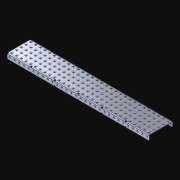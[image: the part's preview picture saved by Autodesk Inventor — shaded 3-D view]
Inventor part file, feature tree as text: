
AUTODESK INVENTOR PART (.ipt)
format: ipt  version: 2021 (Build 250183000, 183)  size: 2,331,648 bytes
history: native  units: in
note: dims shown in document units (in); Inventor stores cm internally (conversion verified against a paired STEP export)
features: extrude x211, other x211, sketch x4, pattern_linear x3
ambient origin geometry x8: Origin, YZ Plane, XZ Plane, XY Plane, X Axis, Y Axis, Z Axis, Center Point
bodies: Solid1 (feature_tree)
feature tree (429):
  pattern_linear  "Rectangular Pattern1"  Spacing1=0.182in  [1 undecoded]
  pattern_linear  "Rectangular Pattern2"  Spacing1=0.046in  [1 undecoded]
  pattern_linear  "Rectangular Pattern3"  Spacing1=0.5in  [1 undecoded]
  extrude  "Extrusion1"  Depth=0.046in
  sketch  "Sketch1"  dims[d0=0.182in]
  other  "Srf1"
  sketch  "Sketch2"  dims[d1=0.046in d2=0.0in]
  other  "Srf2"
  sketch  "Sketch3"  dims[d3=0.182in]
  other  "Srf3"
  other  "Srf4"
  other  "Srf5"
  other  "Srf6"
  other  "Srf7"
  other  "Srf8"
  other  "Srf9"
  other  "Srf10"
  other  "Srf11"
  other  "Srf12"
  other  "Srf13"
  other  "Srf14"
  other  "Srf15"
  other  "Srf16"
  other  "Srf17"
  other  "Srf18"
  other  "Srf19"
  other  "Srf20"
  other  "Srf21"
  other  "Srf22"
  other  "Srf23"
  other  "Srf24"
  other  "Srf25"
  other  "Srf26"
  other  "Srf27"
  other  "Srf28"
  other  "Srf29"
  other  "Srf30"
  other  "Srf31"
  other  "Srf32"
  other  "Srf38"
  other  "Srf39"
  other  "Srf40"
  other  "Srf41"
  other  "Srf42"
  other  "Srf43"
  other  "Srf44"
  other  "Srf45"
  other  "Srf46"
  other  "Srf47"
  other  "Srf48"
  other  "Srf49"
  other  "Srf50"
  other  "Srf51"
  other  "Srf52"
  other  "Srf53"
  other  "Srf54"
  other  "Srf55"
  other  "Srf56"
  other  "Srf57"
  other  "Srf58"
  other  "Srf59"
  other  "Srf60"
  other  "Srf61"
  other  "Srf62"
  other  "Srf63"
  other  "Srf64"
  other  "Srf65"
  other  "Srf66"
  other  "Srf72"
  other  "Srf73"
  other  "Srf74"
  other  "Srf75"
  other  "Srf76"
  other  "Srf77"
  other  "Srf78"
  other  "Srf79"
  other  "Srf80"
  other  "Srf81"
  other  "Srf82"
  other  "Srf83"
  other  "Srf84"
  other  "Srf85"
  other  "Srf86"
  other  "Srf87"
  other  "Srf88"
  other  "Srf89"
  other  "Srf90"
  other  "Srf91"
  other  "Srf92"
  other  "Srf93"
  other  "Srf94"
  other  "Srf95"
  other  "Srf96"
  other  "Srf97"
  other  "Srf98"
  other  "Srf99"
  other  "Srf100"
  other  "Srf101"
  other  "Srf107"
  other  "Srf108"
  other  "Srf109"
  other  "Srf110"
  other  "Srf111"
  other  "Srf112"
  other  "Srf113"
  other  "Srf114"
  other  "Srf115"
  other  "Srf116"
  other  "Srf117"
  other  "Srf118"
  other  "Srf119"
  other  "Srf120"
  other  "Srf121"
  other  "Srf122"
  other  "Srf123"
  other  "Srf124"
  other  "Srf125"
  other  "Srf126"
  other  "Srf127"
  other  "Srf128"
  other  "Srf129"
  other  "Srf130"
  other  "Srf131"
  other  "Srf132"
  other  "Srf133"
  other  "Srf134"
  other  "Srf135"
  other  "Srf136"
  other  "Srf142"
  other  "Srf143"
  other  "Srf144"
  other  "Srf145"
  other  "Srf146"
  other  "Srf147"
  other  "Srf148"
  other  "Srf149"
  other  "Srf150"
  other  "Srf151"
  other  "Srf152"
  other  "Srf153"
  other  "Srf154"
  other  "Srf155"
  other  "Srf156"
  other  "Srf157"
  other  "Srf158"
  other  "Srf159"
  other  "Srf160"
  other  "Srf161"
  other  "Srf162"
  other  "Srf163"
  other  "Srf164"
  other  "Srf165"
  other  "Srf166"
  other  "Srf167"
  other  "Srf168"
  other  "Srf169"
  other  "Srf170"
  other  "Srf171"
  other  "Srf177"
  other  "Srf178"
  other  "Srf179"
  other  "Srf180"
  other  "Srf181"
  other  "Srf182"
  other  "Srf183"
  other  "Srf184"
  other  "Srf185"
  other  "Srf186"
  other  "Srf187"
  other  "Srf188"
  other  "Srf189"
  other  "Srf190"
  other  "Srf191"
  other  "Srf192"
  other  "Srf193"
  other  "Srf194"
  other  "Srf195"
  other  "Srf196"
  other  "Srf197"
  other  "Srf198"
  other  "Srf199"
  other  "Srf200"
  other  "Srf201"
  other  "Srf202"
  other  "Srf203"
  other  "Srf204"
  other  "Srf205"
  other  "Srf206"
  other  "Srf212"
  other  "Srf213"
  other  "Srf214"
  other  "Srf215"
  other  "Srf216"
  other  "Srf217"
  other  "Srf218"
  other  "Srf219"
  other  "Srf220"
  other  "Srf221"
  other  "Srf222"
  other  "Srf223"
  other  "Srf224"
  other  "Srf225"
  other  "Srf226"
  other  "Srf227"
  other  "Srf228"
  other  "Srf229"
  other  "Srf230"
  other  "Srf231"
  other  "Srf232"
  other  "Srf233"
  other  "Srf234"
  other  "Srf235"
  other  "Srf236"
  other  "Srf237"
  other  "Srf238"
  other  "Srf239"
  other  "Srf240"
  sketch  "Sketch4"  dims[d4=0.046in d5=0.0in d6=0.182in d7=0.046in d8=0.0in d11=0.5in d12=11.811in d14=0.5in d15=1.9685in d17=0.5in d18=11.811in d20=0.5in d21=2.5in d22=0.0in]
  parser-record x1  (decoder bookkeeping rows leaked as tree rows — omitted from the tree; the rows remain in map.json)
  extrude  "ExtrusionSrf1"  Depth=0.046in
  extrude  "ExtrusionSrf2"  Depth=0.046in
  extrude  "ExtrusionSrf3"  Depth=0.046in
  extrude  "ExtrusionSrf4"  Depth=0.046in
  extrude  "ExtrusionSrf5"  Depth=0.046in
  extrude  "ExtrusionSrf6"  TaperAngle=0.0deg  [1 undecoded]
  extrude  "ExtrusionSrf7"  [1 undecoded]
  extrude  "ExtrusionSrf8"  [1 undecoded]
  extrude  "ExtrusionSrf9"  [1 undecoded]
  extrude  "ExtrusionSrf10"  [1 undecoded]
  extrude  "ExtrusionSrf11"  [1 undecoded]
  extrude  "ExtrusionSrf12"  [1 undecoded]
  extrude  "ExtrusionSrf13"  [1 undecoded]
  extrude  "ExtrusionSrf14"  [1 undecoded]
  extrude  "ExtrusionSrf15"  [1 undecoded]
  extrude  "ExtrusionSrf16"  [1 undecoded]
  extrude  "ExtrusionSrf17"  [1 undecoded]
  extrude  "ExtrusionSrf18"  [1 undecoded]
  extrude  "ExtrusionSrf19"  [1 undecoded]
  extrude  "ExtrusionSrf20"  [1 undecoded]
  extrude  "ExtrusionSrf21"  [1 undecoded]
  extrude  "ExtrusionSrf22"  [1 undecoded]
  extrude  "ExtrusionSrf23"  [1 undecoded]
  extrude  "ExtrusionSrf24"  [1 undecoded]
  extrude  "ExtrusionSrf25"  [1 undecoded]
  extrude  "ExtrusionSrf26"  [1 undecoded]
  extrude  "ExtrusionSrf27"  [1 undecoded]
  extrude  "ExtrusionSrf28"  [1 undecoded]
  extrude  "ExtrusionSrf29"  [1 undecoded]
  extrude  "ExtrusionSrf30"  [1 undecoded]
  extrude  "ExtrusionSrf31"  [1 undecoded]
  extrude  "ExtrusionSrf32"  [1 undecoded]
  extrude  "ExtrusionSrf38"  [1 undecoded]
  extrude  "ExtrusionSrf39"  [1 undecoded]
  extrude  "ExtrusionSrf40"  [1 undecoded]
  extrude  "ExtrusionSrf41"  [1 undecoded]
  extrude  "ExtrusionSrf42"  [1 undecoded]
  extrude  "ExtrusionSrf43"  [1 undecoded]
  extrude  "ExtrusionSrf44"  [1 undecoded]
  extrude  "ExtrusionSrf45"  [1 undecoded]
  extrude  "ExtrusionSrf46"  [1 undecoded]
  extrude  "ExtrusionSrf47"  [1 undecoded]
  extrude  "ExtrusionSrf48"  [1 undecoded]
  extrude  "ExtrusionSrf49"  [1 undecoded]
  extrude  "ExtrusionSrf50"  [1 undecoded]
  extrude  "ExtrusionSrf51"  [1 undecoded]
  extrude  "ExtrusionSrf52"  [1 undecoded]
  extrude  "ExtrusionSrf53"  [1 undecoded]
  extrude  "ExtrusionSrf54"  [1 undecoded]
  extrude  "ExtrusionSrf55"  [1 undecoded]
  extrude  "ExtrusionSrf56"  [1 undecoded]
  extrude  "ExtrusionSrf57"  [1 undecoded]
  extrude  "ExtrusionSrf58"  [1 undecoded]
  extrude  "ExtrusionSrf59"  [1 undecoded]
  extrude  "ExtrusionSrf60"  [1 undecoded]
  extrude  "ExtrusionSrf61"  [1 undecoded]
  extrude  "ExtrusionSrf62"  [1 undecoded]
  extrude  "ExtrusionSrf63"  [1 undecoded]
  extrude  "ExtrusionSrf64"  [1 undecoded]
  extrude  "ExtrusionSrf65"  [1 undecoded]
  extrude  "ExtrusionSrf66"  [1 undecoded]
  extrude  "ExtrusionSrf72"  [1 undecoded]
  extrude  "ExtrusionSrf73"  [1 undecoded]
  extrude  "ExtrusionSrf74"  [1 undecoded]
  extrude  "ExtrusionSrf75"  [1 undecoded]
  extrude  "ExtrusionSrf76"  [1 undecoded]
  extrude  "ExtrusionSrf77"  [1 undecoded]
  extrude  "ExtrusionSrf78"  [1 undecoded]
  extrude  "ExtrusionSrf79"  [1 undecoded]
  extrude  "ExtrusionSrf80"  [1 undecoded]
  extrude  "ExtrusionSrf81"  [1 undecoded]
  extrude  "ExtrusionSrf82"  [1 undecoded]
  extrude  "ExtrusionSrf83"  [1 undecoded]
  extrude  "ExtrusionSrf84"  [1 undecoded]
  extrude  "ExtrusionSrf85"  [1 undecoded]
  extrude  "ExtrusionSrf86"  [1 undecoded]
  extrude  "ExtrusionSrf87"  [1 undecoded]
  extrude  "ExtrusionSrf88"  [1 undecoded]
  extrude  "ExtrusionSrf89"  [1 undecoded]
  extrude  "ExtrusionSrf90"  [1 undecoded]
  extrude  "ExtrusionSrf91"  [1 undecoded]
  extrude  "ExtrusionSrf92"  [1 undecoded]
  extrude  "ExtrusionSrf93"  [1 undecoded]
  extrude  "ExtrusionSrf94"  [1 undecoded]
  extrude  "ExtrusionSrf95"  [1 undecoded]
  extrude  "ExtrusionSrf96"  [1 undecoded]
  extrude  "ExtrusionSrf97"  [1 undecoded]
  extrude  "ExtrusionSrf98"  [1 undecoded]
  extrude  "ExtrusionSrf99"  [1 undecoded]
  extrude  "ExtrusionSrf100"  [1 undecoded]
  extrude  "ExtrusionSrf101"  [1 undecoded]
  extrude  "ExtrusionSrf107"  [1 undecoded]
  extrude  "ExtrusionSrf108"  [1 undecoded]
  extrude  "ExtrusionSrf109"  [1 undecoded]
  extrude  "ExtrusionSrf110"  [1 undecoded]
  extrude  "ExtrusionSrf111"  [1 undecoded]
  extrude  "ExtrusionSrf112"  [1 undecoded]
  extrude  "ExtrusionSrf113"  [1 undecoded]
  extrude  "ExtrusionSrf114"  [1 undecoded]
  extrude  "ExtrusionSrf115"  [1 undecoded]
  extrude  "ExtrusionSrf116"  [1 undecoded]
  extrude  "ExtrusionSrf117"  [1 undecoded]
  extrude  "ExtrusionSrf118"  [1 undecoded]
  extrude  "ExtrusionSrf119"  [1 undecoded]
  extrude  "ExtrusionSrf120"  [1 undecoded]
  extrude  "ExtrusionSrf121"  [1 undecoded]
  extrude  "ExtrusionSrf122"  [1 undecoded]
  extrude  "ExtrusionSrf123"  [1 undecoded]
  extrude  "ExtrusionSrf124"  [1 undecoded]
  extrude  "ExtrusionSrf125"  [1 undecoded]
  extrude  "ExtrusionSrf126"  [1 undecoded]
  extrude  "ExtrusionSrf127"  [1 undecoded]
  extrude  "ExtrusionSrf128"  [1 undecoded]
  extrude  "ExtrusionSrf129"  [1 undecoded]
  extrude  "ExtrusionSrf130"  [1 undecoded]
  extrude  "ExtrusionSrf131"  [1 undecoded]
  extrude  "ExtrusionSrf132"  [1 undecoded]
  extrude  "ExtrusionSrf133"  [1 undecoded]
  extrude  "ExtrusionSrf134"  [1 undecoded]
  extrude  "ExtrusionSrf135"  [1 undecoded]
  extrude  "ExtrusionSrf136"  [1 undecoded]
  extrude  "ExtrusionSrf142"  [1 undecoded]
  extrude  "ExtrusionSrf143"  [1 undecoded]
  extrude  "ExtrusionSrf144"  [1 undecoded]
  extrude  "ExtrusionSrf145"  [1 undecoded]
  extrude  "ExtrusionSrf146"  [1 undecoded]
  extrude  "ExtrusionSrf147"  [1 undecoded]
  extrude  "ExtrusionSrf148"  [1 undecoded]
  extrude  "ExtrusionSrf149"  [1 undecoded]
  extrude  "ExtrusionSrf150"  [1 undecoded]
  extrude  "ExtrusionSrf151"  [1 undecoded]
  extrude  "ExtrusionSrf152"  [1 undecoded]
  extrude  "ExtrusionSrf153"  [1 undecoded]
  extrude  "ExtrusionSrf154"  [1 undecoded]
  extrude  "ExtrusionSrf155"  [1 undecoded]
  extrude  "ExtrusionSrf156"  [1 undecoded]
  extrude  "ExtrusionSrf157"  [1 undecoded]
  extrude  "ExtrusionSrf158"  [1 undecoded]
  extrude  "ExtrusionSrf159"  [1 undecoded]
  extrude  "ExtrusionSrf160"  [1 undecoded]
  extrude  "ExtrusionSrf161"  [1 undecoded]
  extrude  "ExtrusionSrf162"  [1 undecoded]
  extrude  "ExtrusionSrf163"  [1 undecoded]
  extrude  "ExtrusionSrf164"  [1 undecoded]
  extrude  "ExtrusionSrf165"  [1 undecoded]
  extrude  "ExtrusionSrf166"  [1 undecoded]
  extrude  "ExtrusionSrf167"  [1 undecoded]
  extrude  "ExtrusionSrf168"  [1 undecoded]
  extrude  "ExtrusionSrf169"  [1 undecoded]
  extrude  "ExtrusionSrf170"  [1 undecoded]
  extrude  "ExtrusionSrf171"  [1 undecoded]
  extrude  "ExtrusionSrf177"  [1 undecoded]
  extrude  "ExtrusionSrf178"  [1 undecoded]
  extrude  "ExtrusionSrf179"  [1 undecoded]
  extrude  "ExtrusionSrf180"  [1 undecoded]
  extrude  "ExtrusionSrf181"  [1 undecoded]
  extrude  "ExtrusionSrf182"  [1 undecoded]
  extrude  "ExtrusionSrf183"  [1 undecoded]
  extrude  "ExtrusionSrf184"  [1 undecoded]
  extrude  "ExtrusionSrf185"  [1 undecoded]
  extrude  "ExtrusionSrf186"  [1 undecoded]
  extrude  "ExtrusionSrf187"  [1 undecoded]
  extrude  "ExtrusionSrf188"  [1 undecoded]
  extrude  "ExtrusionSrf189"  [1 undecoded]
  extrude  "ExtrusionSrf190"  [1 undecoded]
  extrude  "ExtrusionSrf191"  [1 undecoded]
  extrude  "ExtrusionSrf192"  [1 undecoded]
  extrude  "ExtrusionSrf193"  [1 undecoded]
  extrude  "ExtrusionSrf194"  [1 undecoded]
  extrude  "ExtrusionSrf195"  [1 undecoded]
  extrude  "ExtrusionSrf196"  [1 undecoded]
  extrude  "ExtrusionSrf197"  [1 undecoded]
  extrude  "ExtrusionSrf198"  [1 undecoded]
  extrude  "ExtrusionSrf199"  [1 undecoded]
  extrude  "ExtrusionSrf200"  [1 undecoded]
  extrude  "ExtrusionSrf201"  [1 undecoded]
  extrude  "ExtrusionSrf202"  [1 undecoded]
  extrude  "ExtrusionSrf203"  [1 undecoded]
  extrude  "ExtrusionSrf204"  [1 undecoded]
  extrude  "ExtrusionSrf205"  [1 undecoded]
  extrude  "ExtrusionSrf206"  [1 undecoded]
  extrude  "ExtrusionSrf212"  [1 undecoded]
  extrude  "ExtrusionSrf213"  [1 undecoded]
  extrude  "ExtrusionSrf214"  [1 undecoded]
  extrude  "ExtrusionSrf215"  [1 undecoded]
  extrude  "ExtrusionSrf216"  [1 undecoded]
  extrude  "ExtrusionSrf217"  [1 undecoded]
  extrude  "ExtrusionSrf218"  [1 undecoded]
  extrude  "ExtrusionSrf219"  [1 undecoded]
  extrude  "ExtrusionSrf220"  [1 undecoded]
  extrude  "ExtrusionSrf221"  [1 undecoded]
  extrude  "ExtrusionSrf222"  [1 undecoded]
  extrude  "ExtrusionSrf223"  [1 undecoded]
  extrude  "ExtrusionSrf224"  [1 undecoded]
  extrude  "ExtrusionSrf225"  [1 undecoded]
  extrude  "ExtrusionSrf226"  [1 undecoded]
  extrude  "ExtrusionSrf227"  [1 undecoded]
  extrude  "ExtrusionSrf228"  [1 undecoded]
  extrude  "ExtrusionSrf229"  [1 undecoded]
  extrude  "ExtrusionSrf230"  [1 undecoded]
  extrude  "ExtrusionSrf231"  [1 undecoded]
  extrude  "ExtrusionSrf232"  [1 undecoded]
  extrude  "ExtrusionSrf233"  [1 undecoded]
  extrude  "ExtrusionSrf234"  [1 undecoded]
  extrude  "ExtrusionSrf235"  [1 undecoded]
  extrude  "ExtrusionSrf236"  [1 undecoded]
  extrude  "ExtrusionSrf237"  [1 undecoded]
  extrude  "ExtrusionSrf238"  [1 undecoded]
  extrude  "ExtrusionSrf239"  [1 undecoded]
  extrude  "ExtrusionSrf240"  [1 undecoded]
note: 208 required parameter values undecoded (feature->parameter linkage not recoverable at this tier; creation-order binding heuristic only, values carry confidence <= 0.55)
